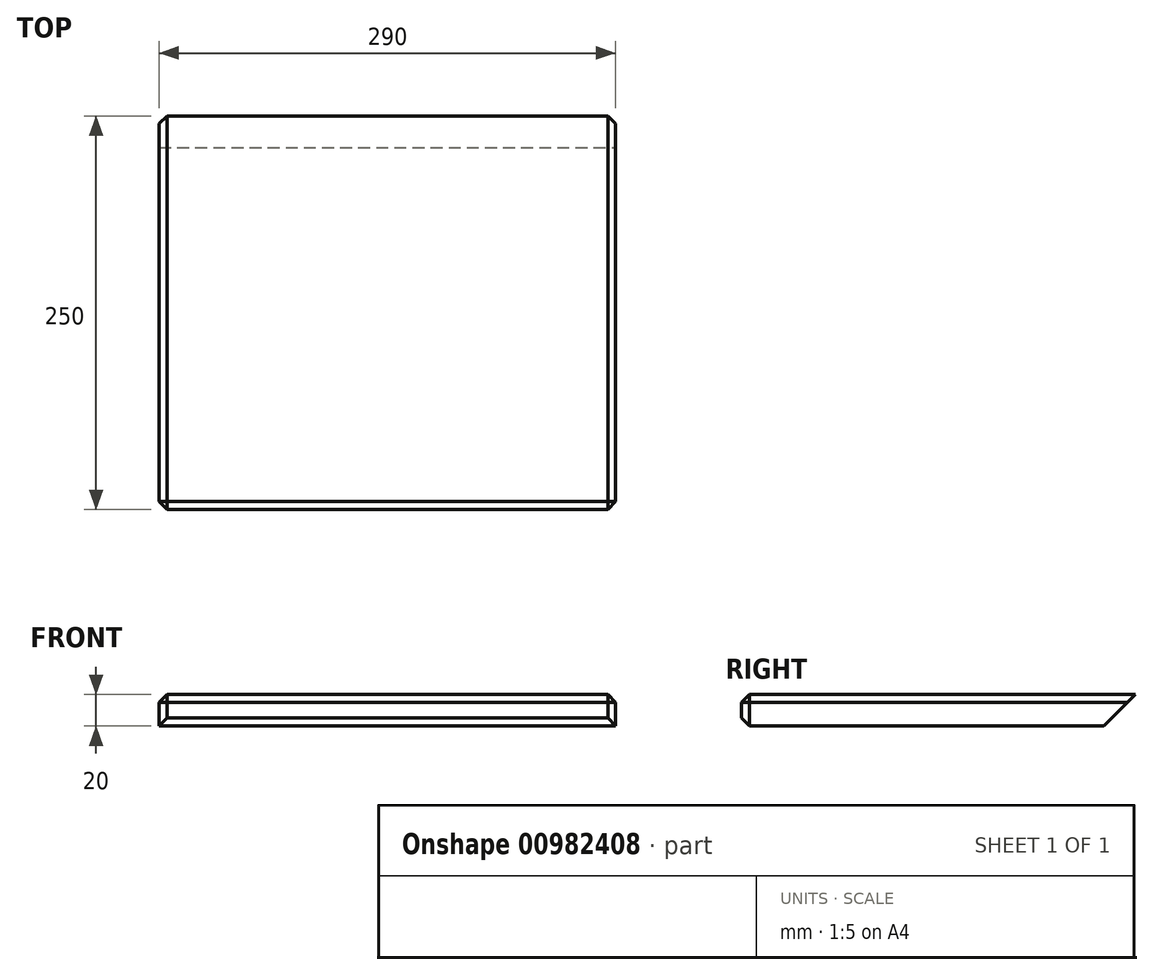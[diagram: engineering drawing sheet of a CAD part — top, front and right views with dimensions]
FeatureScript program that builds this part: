
annotation { "Feature Type Name" : "Feature", "Feature Type Description" : "" }
export const myFeature = defineFeature(function(context is Context, id is Id, definition is map)
    precondition{}
    {
        {
            var Q0;
            Q0=qCreatedBy(makeId("Top.planeOp"),FACE);
            var sketch = newSketch(context, id + "F0", { "sketchPlane" : qUnion([Q0])});
            skLineSegment(sketch, "E0.bottom", {"start": v(145, 125) * mm, "end": v(-145, 125) * mm});
            skLineSegment(sketch, "E0.top", {"start": v(145, -125) * mm, "end": v(-145, -125) * mm});
            skLineSegment(sketch, "E0.left", {"start": v(145, 125) * mm, "end": v(145, -125) * mm});
            skLineSegment(sketch, "E0.right", {"start": v(-145, 125) * mm, "end": v(-145, -125) * mm});
            skPoint(sketch, "E0.middle", {"position": v(0, 0) * mm});
            skSolve(sketch);
        }
        {
            var Q0;
            Q0 = qSketchRegion(id + "F0", true);
            extrude(context, id + "F1", {"entities" : qUnion([Q0]), "depth" : 20 * mm, "offsetDistance" : 25 * mm});
        }
        {
            var Q0;
            Q0=makeQuery(id+"F1.opExtrude","CAP_EDGE",EDGE,{"disambiguationData":[OSD([sQuery(id+"F0.wireOp",EDGE,"E0.bottom")])],"isStart":true});
            chamfer(context, id + "F2", {"entities" : qUnion([Q0]), "width" : 20 * mm, "tangentPropagation" : true});
        }
        {
            var Q0;
            Q0=makeQuery(id+"F1.opExtrude","CAP_EDGE",EDGE,{"disambiguationData":[OSD([sQuery(id+"F0.wireOp",EDGE,"E0.top")])],"isStart":false});
            var Q1;
            Q1=makeQuery(id+"F1.opExtrude","CAP_EDGE",EDGE,{"disambiguationData":[OSD([sQuery(id+"F0.wireOp",EDGE,"E0.top")])],"isStart":true});
            var Q2;
            Q2=makeQuery(id+"F1.opExtrude","CAP_EDGE",EDGE,{"disambiguationData":[OSD([sQuery(id+"F0.wireOp",EDGE,"E0.left")])],"isStart":false});
            var Q3;
            Q3=makeQuery(id+"F1.opExtrude","SWEPT_EDGE",EDGE,{"disambiguationData":[OSD([sQuery(id+"F0.wireOp",EDGE,"E0.top"),sQuery(id+"F0.wireOp",EDGE,"E0.left")])]});
            var Q4;
            Q4=makeQuery(id+"F1.opExtrude","SWEPT_EDGE",EDGE,{"disambiguationData":[OSD([sQuery(id+"F0.wireOp",EDGE,"E0.top"),sQuery(id+"F0.wireOp",EDGE,"E0.right")])]});
            var Q5;
            Q5=makeQuery(id+"F1.opExtrude","CAP_EDGE",EDGE,{"disambiguationData":[OSD([sQuery(id+"F0.wireOp",EDGE,"E0.right")])],"isStart":false});
            chamfer(context, id + "F3", {"entities" : qUnion([Q0, Q1, Q2, Q3, Q4, Q5]), "width" : 5 * mm, "tangentPropagation" : true});
        }
    });
